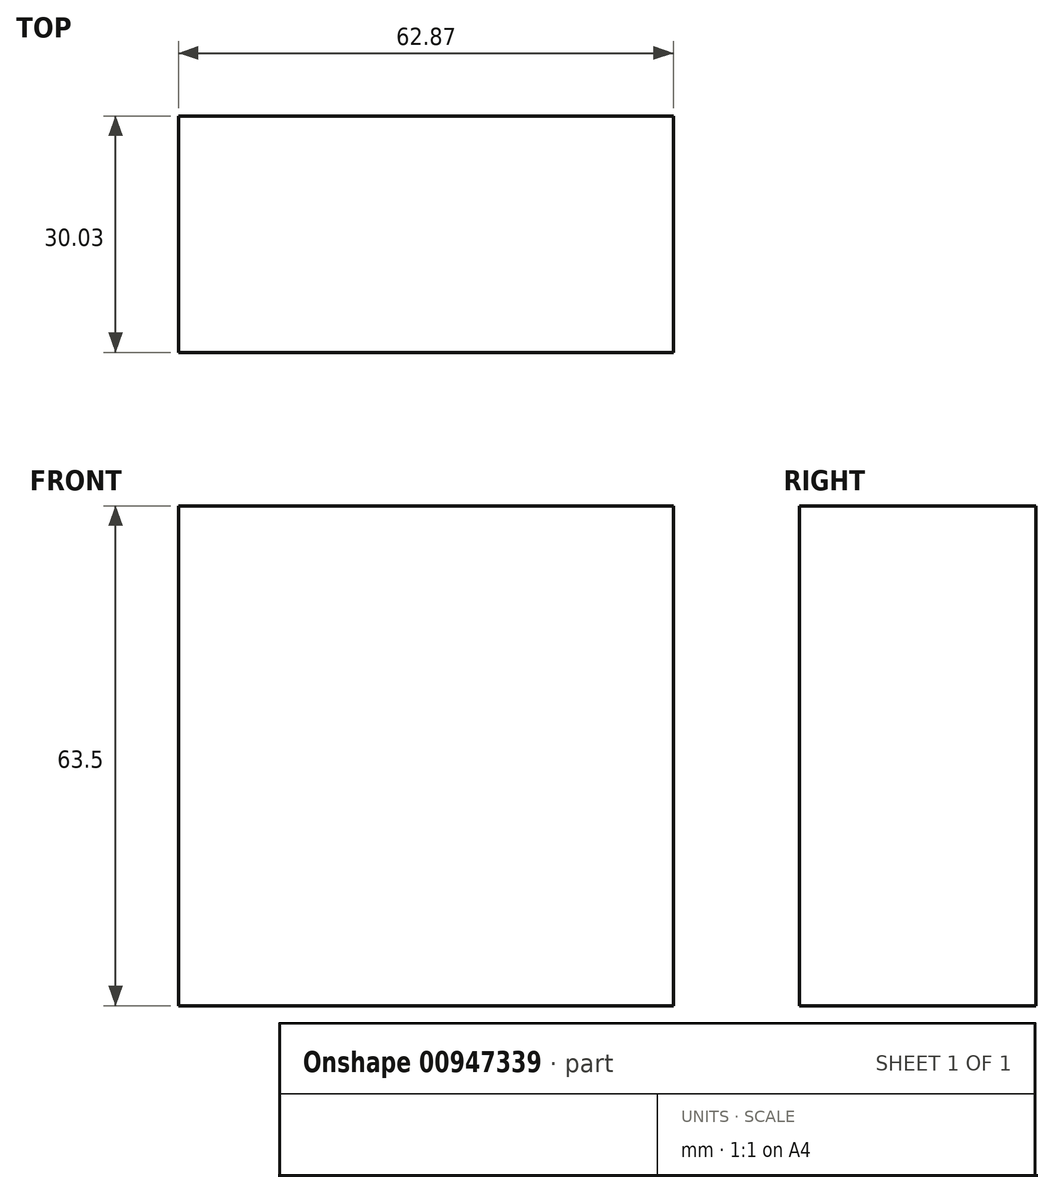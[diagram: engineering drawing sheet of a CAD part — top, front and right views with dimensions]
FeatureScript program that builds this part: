
annotation { "Feature Type Name" : "Feature", "Feature Type Description" : "" }
export const myFeature = defineFeature(function(context is Context, id is Id, definition is map)
    precondition{}
    {
        {
            var Q0;
            Q0=qCreatedBy(makeId("Top.planeOp"),FACE);
            var sketch = newSketch(context, id + "F0", { "sketchPlane" : qUnion([Q0])});
            skLineSegment(sketch, "E0.bottom", {"start": v(-30.16, 14.8) * mm, "end": v(32.71, 14.8) * mm});
            skLineSegment(sketch, "E0.top", {"start": v(-30.16, -15.23) * mm, "end": v(32.71, -15.23) * mm});
            skLineSegment(sketch, "E0.left", {"start": v(-30.16, 14.8) * mm, "end": v(-30.16, -15.23) * mm});
            skLineSegment(sketch, "E0.right", {"start": v(32.71, 14.8) * mm, "end": v(32.71, -15.23) * mm});
            skSolve(sketch);
        }
        {
            var Q0;
            Q0=makeQuery(id+"F0.imprint","IMPRINT",FACE,{"disambiguationData":[TD([[makeQuery(id+"F0.imprint","IMPRINT",EDGE,{"derivedFrom":sQuery(id+"F0.wireOp",EDGE,"E0.bottom")}),-1.0]])]});
            extrude(context, id + "F1", {"entities" : qUnion([Q0]), "depth" : 63.5 * mm, "offsetDistance" : 25.4 * mm});
        }
    });
